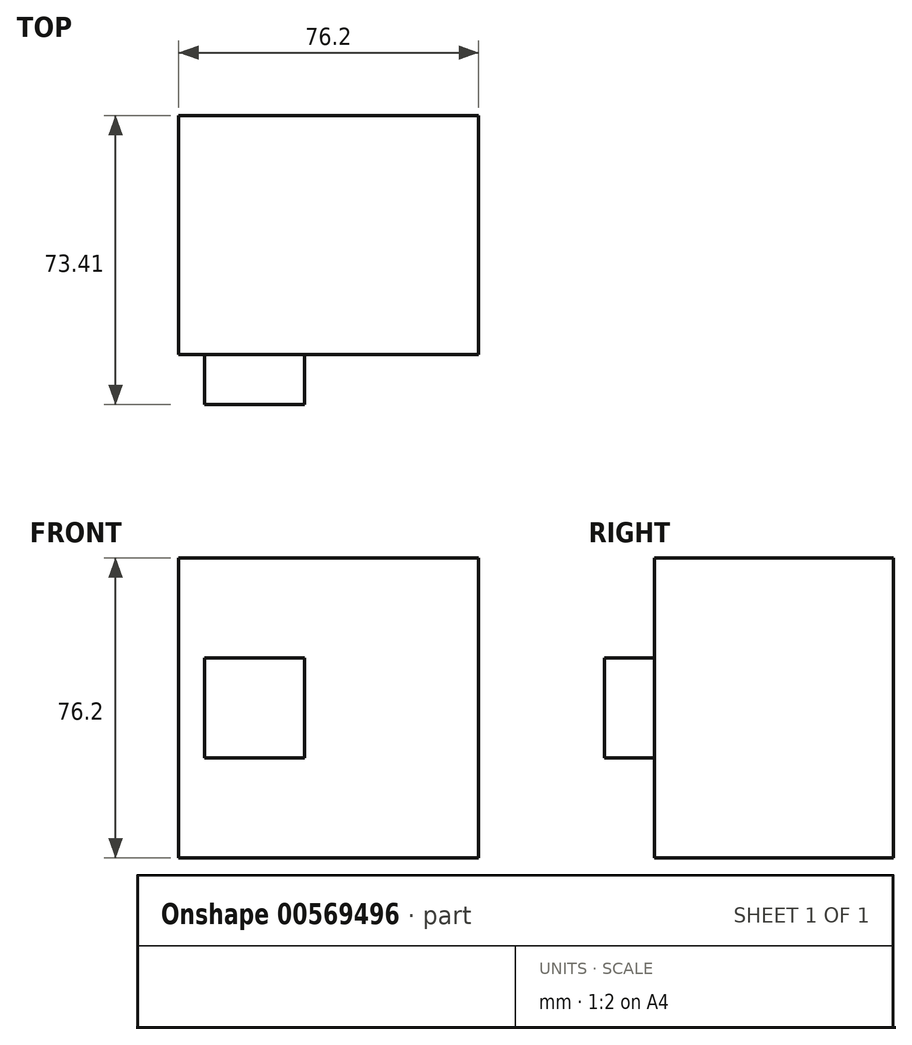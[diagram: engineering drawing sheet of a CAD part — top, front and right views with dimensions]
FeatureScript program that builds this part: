
annotation { "Feature Type Name" : "Feature", "Feature Type Description" : "" }
export const myFeature = defineFeature(function(context is Context, id is Id, definition is map)
    precondition{}
    {
        {
            var Q0;
            Q0=qCreatedBy(makeId("Front.planeOp"),FACE);
            var sketch = newSketch(context, id + "F0", { "sketchPlane" : qUnion([Q0])});
            skLineSegment(sketch, "E0.bottom", {"start": v(-76.2, 79.97) * mm, "end": v(0, 79.97) * mm});
            skLineSegment(sketch, "E0.top", {"start": v(-76.2, 3.77) * mm, "end": v(0, 3.77) * mm});
            skLineSegment(sketch, "E0.left", {"start": v(-76.2, 79.97) * mm, "end": v(-76.2, 3.77) * mm});
            skLineSegment(sketch, "E0.right", {"start": v(0, 79.97) * mm, "end": v(0, 3.77) * mm});
            skSolve(sketch);
        }
        {
            var Q0;
            Q0 = qSketchRegion(id + "F0", true);
            extrude(context, id + "F1", {"entities" : qUnion([Q0]), "depth" : 25.4 * mm, "offsetDistance" : 25.4 * mm});
        }
        {
            var Q0;
            Q0=makeQuery(id+"F0.imprint","IMPRINT",FACE,{"disambiguationData":[TD([[makeQuery(id+"F0.imprint","IMPRINT",EDGE,{"derivedFrom":sQuery(id+"F0.wireOp",EDGE,"E0.bottom")}),-1.0]])]});
            var Q1;
            Q1=makeQuery(id+"F1.opExtrude","CAP_FACE",FACE,{"disambiguationData":[OSD([sQuery(id+"F0.wireOp",EDGE,"E0.bottom"),sQuery(id+"F0.wireOp",EDGE,"E0.top"),sQuery(id+"F0.wireOp",EDGE,"E0.left"),sQuery(id+"F0.wireOp",EDGE,"E0.right")])],"isStart":false});
            var Q2;
            Q2=makeQuery(id+"F1.opExtrude","CAP_FACE",FACE,{"disambiguationData":[OSD([sQuery(id+"F0.wireOp",EDGE,"E0.bottom"),sQuery(id+"F0.wireOp",EDGE,"E0.top"),sQuery(id+"F0.wireOp",EDGE,"E0.left"),sQuery(id+"F0.wireOp",EDGE,"E0.right")])],"isStart":true});
            extrude(context, id + "F2", {"entities" : qUnion([Q0, Q1, Q2]), "operationType" : NewBodyOperationType.ADD, "depth" : 35.3 * mm, "offsetDistance" : 25.4 * mm});
        }
        {
            var Q0;
            {var subQ0=sQuery(id+"F0.wireOp",EDGE,"E0.right");var subQ1=sQuery(id+"F0.wireOp",EDGE,"E0.left");var subQ2=sQuery(id+"F0.wireOp",EDGE,"E0.top");var subQ3=sQuery(id+"F0.wireOp",EDGE,"E0.bottom");Q0=makeQuery(id+"F2.opExtrude","CAP_FACE",FACE,{"disambiguationData":[OSD([subQ3,subQ2,subQ1,subQ0]),TDD([makeQuery(id+"F1.opExtrude","CAP_FACE",FACE,{"disambiguationData":[OSD([subQ3,subQ2,subQ1,subQ0])],"isStart":false})])],"isStart":false});}
            var sketch = newSketch(context, id + "F3", { "sketchPlane" : qUnion([Q0])});
            skLineSegment(sketch, "E1.bottom", {"start": v(-44.26, 54.57) * mm, "end": v(-69.66, 54.57) * mm});
            skLineSegment(sketch, "E1.top", {"start": v(-44.26, 29.17) * mm, "end": v(-69.66, 29.17) * mm});
            skLineSegment(sketch, "E1.left", {"start": v(-44.26, 54.57) * mm, "end": v(-44.26, 29.17) * mm});
            skLineSegment(sketch, "E1.right", {"start": v(-69.66, 54.57) * mm, "end": v(-69.66, 29.17) * mm});
            skLineSegment(sketch, "E2.bottom", {"start": v(-56.96, 54.57) * mm, "end": v(-60.4, 54.57) * mm});
            skLineSegment(sketch, "E2.top", {"start": v(-56.96, 54.57) * mm, "end": v(-60.4, 54.57) * mm});
            skLineSegment(sketch, "E2.left", {"start": v(-56.96, 54.57) * mm, "end": v(-56.96, 54.57) * mm});
            skLineSegment(sketch, "E2.right", {"start": v(-60.4, 54.57) * mm, "end": v(-60.4, 54.57) * mm});
            skSolve(sketch);
        }
        {
            var Q0;
            Q0=makeQuery(id+"F3.imprint","IMPRINT",FACE,{"disambiguationData":[TD([[makeQuery(id+"F3.imprint","IMPRINT",EDGE,{"derivedFrom":sQuery(id+"F3.wireOp",EDGE,"E1.top")}),-1.0]])]});
            extrude(context, id + "F4", {"entities" : qUnion([Q0]), "operationType" : NewBodyOperationType.ADD, "depth" : 12.7 * mm, "offsetDistance" : 25.4 * mm});
        }
    });
